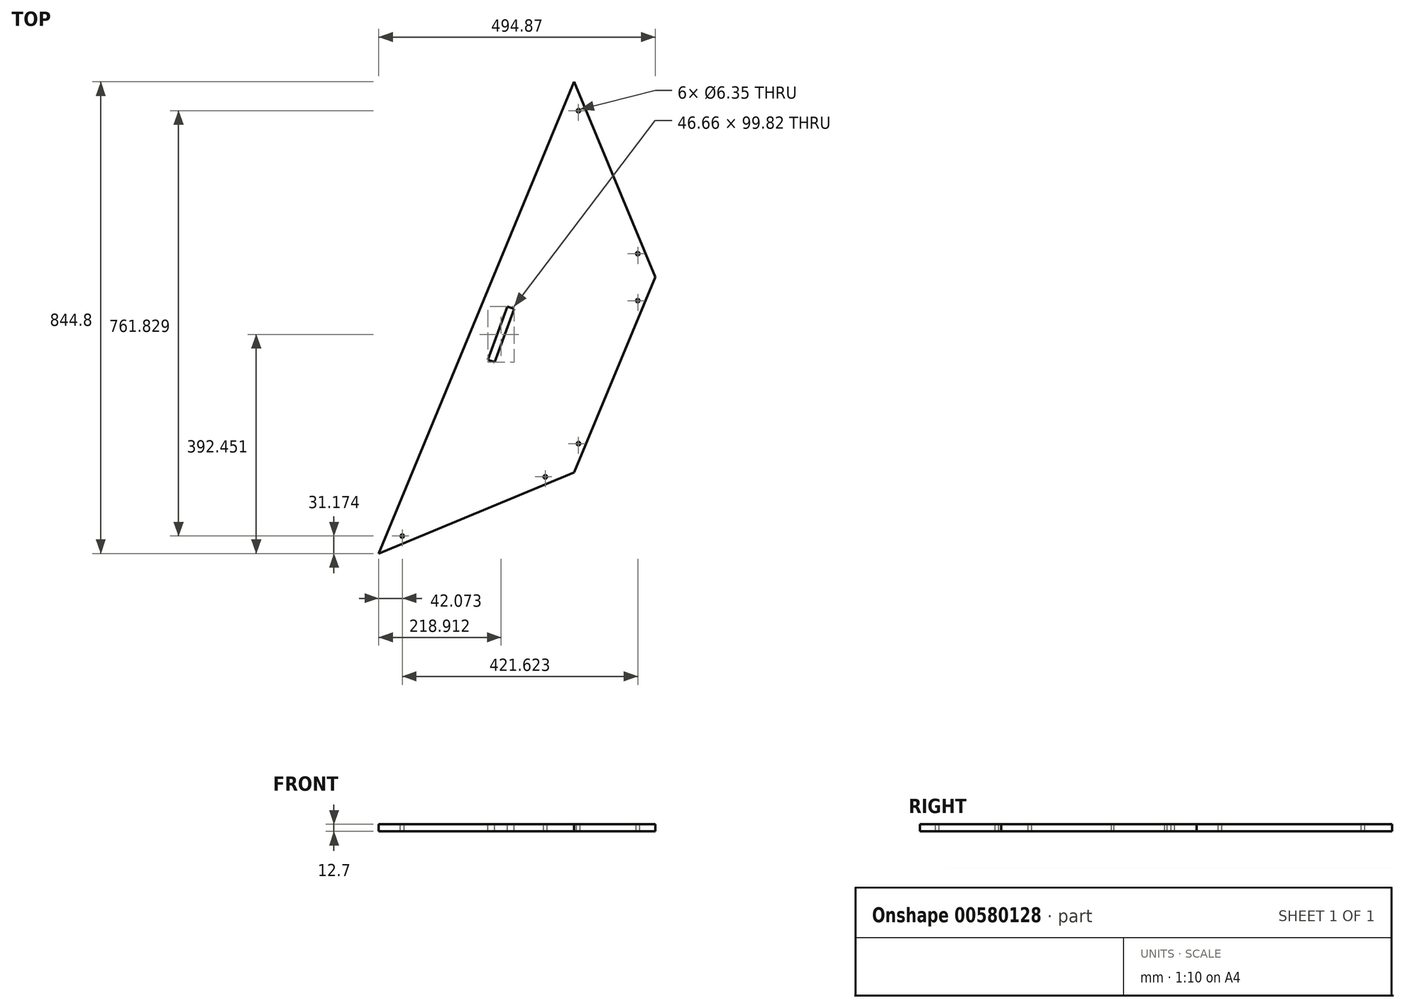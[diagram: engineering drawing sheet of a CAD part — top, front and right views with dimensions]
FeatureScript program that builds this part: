
annotation { "Feature Type Name" : "Feature", "Feature Type Description" : "" }
export const myFeature = defineFeature(function(context is Context, id is Id, definition is map)
    precondition{}
    {
        {
            var Q0;
            Q0=qCreatedBy(makeId("Top.planeOp"),FACE);
            var sketch = newSketch(context, id + "F0", { "sketchPlane" : qUnion([Q0])});
            skCircle(sketch, "E0.cCircle", {"center": v(0, 0) * mm, "radius": 494.87 * mm, "construction": true});
            skLineSegment(sketch, "E0.0", {"start": v(494.87, 0) * mm, "end": v(349.93, -349.93) * mm});
            skLineSegment(sketch, "E0.1", {"start": v(349.93, -349.93) * mm, "end": v(0, -494.87) * mm});
            skLineSegment(sketch, "E0.2", {"start": v(0, -494.87) * mm, "end": v(-349.93, -349.93) * mm});
            skLineSegment(sketch, "E0.3", {"start": v(-349.93, -349.93) * mm, "end": v(-494.87, 0) * mm});
            skLineSegment(sketch, "E0.4", {"start": v(-494.87, 0) * mm, "end": v(-349.93, 349.93) * mm});
            skLineSegment(sketch, "E0.5", {"start": v(-349.93, 349.93) * mm, "end": v(0, 494.87) * mm});
            skLineSegment(sketch, "E0.6", {"start": v(0, 494.87) * mm, "end": v(349.93, 349.93) * mm});
            skLineSegment(sketch, "E0.7", {"start": v(349.93, 349.93) * mm, "end": v(494.87, 0) * mm});
            skLineSegment(sketch, "E1", {"start": v(349.93, 349.93) * mm, "end": v(0, -494.87) * mm});
            skSolve(sketch);
        }
        {
            var Q0;
            Q0=makeQuery(id+"F0.imprint","IMPRINT",FACE,{"disambiguationData":[TD([[makeQuery(id+"F0.imprint","IMPRINT",EDGE,{"derivedFrom":sQuery(id+"F0.wireOp",EDGE,"E0.0")}),-1.0]])]});
            extrude(context, id + "F1", {"entities" : qUnion([Q0]), "depth" : 12.7 * mm, "offsetDistance" : 25.4 * mm});
        }
        {
            var Q0;
            Q0=makeQuery(id+"F1.opExtrude","CAP_FACE",FACE,{"disambiguationData":[OSD([sQuery(id+"F0.wireOp",EDGE,"E0.0"),sQuery(id+"F0.wireOp",EDGE,"E0.1"),sQuery(id+"F0.wireOp",EDGE,"E0.7"),sQuery(id+"F0.wireOp",EDGE,"E1")])],"isStart":false});
            var sketch = newSketch(context, id + "F2", { "sketchPlane" : qUnion([Q0])});
            skCircle(sketch, "E2", {"center": v(42.07, -463.7) * mm, "radius": 3.18 * mm});
            skCircle(sketch, "E3", {"center": v(298.13, -357.63) * mm, "radius": 3.17 * mm});
            skCircle(sketch, "E4", {"center": v(357.63, -298.13) * mm, "radius": 3.17 * mm});
            skCircle(sketch, "E5", {"center": v(463.7, -42.07) * mm, "radius": 3.17 * mm});
            skCircle(sketch, "E6", {"center": v(463.7, 42.07) * mm, "radius": 3.17 * mm});
            skCircle(sketch, "E7", {"center": v(357.63, 298.13) * mm, "radius": 3.18 * mm});
            skLineSegment(sketch, "E8", {"start": v(357.63, 298.13) * mm, "end": v(360.57, 299.35) * mm});
            skLineSegment(sketch, "E9", {"start": v(360.57, 299.35) * mm, "end": v(369.37, 303) * mm});
            skLineSegment(sketch, "E10", {"start": v(463.7, 42.07) * mm, "end": v(466.63, 43.29) * mm});
            skLineSegment(sketch, "E11", {"start": v(466.63, 43.29) * mm, "end": v(475.43, 46.93) * mm});
            skLineSegment(sketch, "E12", {"start": v(463.7, -42.07) * mm, "end": v(460.76, -40.86) * mm});
            skLineSegment(sketch, "E13", {"start": v(298.13, -357.63) * mm, "end": v(299.35, -360.57) * mm});
            skLineSegment(sketch, "E14", {"start": v(299.35, -360.57) * mm, "end": v(303, -369.37) * mm});
            skLineSegment(sketch, "E15", {"start": v(42.07, -463.7) * mm, "end": v(43.29, -466.63) * mm});
            skLineSegment(sketch, "E16", {"start": v(43.29, -466.63) * mm, "end": v(46.93, -475.43) * mm});
            skLineSegment(sketch, "E17", {"start": v(357.63, -298.13) * mm, "end": v(354.7, -296.92) * mm});
            skLineSegment(sketch, "E18", {"start": v(354.7, -296.92) * mm, "end": v(369.37, -303) * mm});
            skLineSegment(sketch, "E19", {"start": v(463.7, -42.07) * mm, "end": v(475.43, -46.93) * mm});
            skSolve(sketch);
        }
        {
            var Q0;
            Q0=qSketchRegion(id+"F2",true);
            extrude(context, id + "F3", {"entities" : qUnion([Q0]), "operationType" : NewBodyOperationType.REMOVE, "endBound" : BoundingType.THROUGH_ALL, "oppositeDirection" : true, "depth" : 25.4 * mm, "offsetDistance" : 25.4 * mm});
        }
        {
            var Q0;
            Q0=makeQuery(id+"F1.opExtrude","CAP_FACE",FACE,{"disambiguationData":[OSD([sQuery(id+"F0.wireOp",EDGE,"E0.0"),sQuery(id+"F0.wireOp",EDGE,"E0.1"),sQuery(id+"F0.wireOp",EDGE,"E0.7"),sQuery(id+"F0.wireOp",EDGE,"E1")])],"isStart":false});
            var sketch = newSketch(context, id + "F4", { "sketchPlane" : qUnion([Q0])});
            skLineSegment(sketch, "E20", {"start": v(195.58, -148) * mm, "end": v(230.3, -52.5) * mm});
            skLineSegment(sketch, "E21", {"start": v(230.3, -52.5) * mm, "end": v(242.24, -56.85) * mm});
            skLineSegment(sketch, "E22", {"start": v(242.24, -56.85) * mm, "end": v(207.52, -152.33) * mm});
            skLineSegment(sketch, "E23", {"start": v(207.52, -152.33) * mm, "end": v(195.58, -148) * mm});
            skSolve(sketch);
        }
        {
            var Q0;
            Q0=makeQuery(id+"F4.imprint","IMPRINT",FACE,{"disambiguationData":[TD([[makeQuery(id+"F4.imprint","IMPRINT",EDGE,{"derivedFrom":sQuery(id+"F4.wireOp",EDGE,"E20")}),-1.0]])]});
            extrude(context, id + "F5", {"entities" : qUnion([Q0]), "operationType" : NewBodyOperationType.REMOVE, "oppositeDirection" : true, "depth" : 25.4 * mm, "offsetDistance" : 25.4 * mm});
        }
    });
